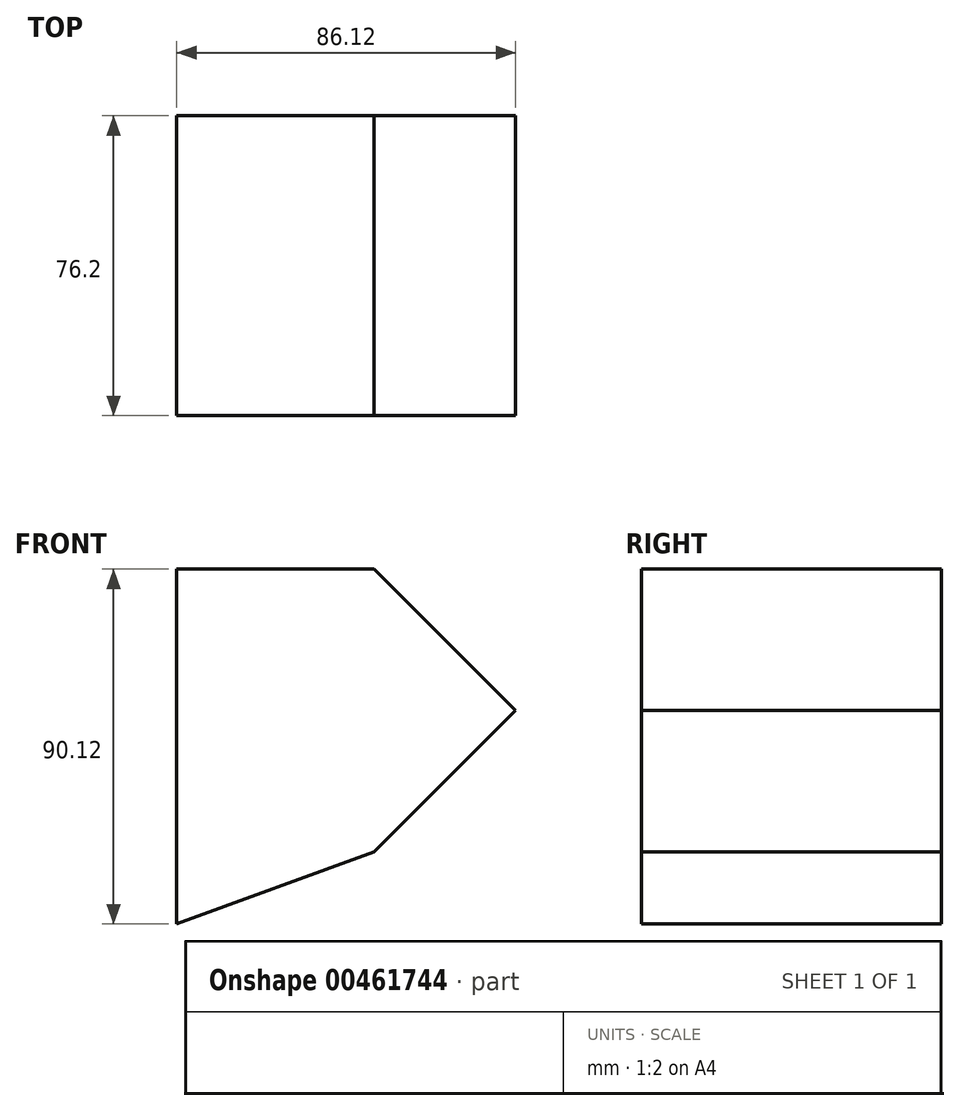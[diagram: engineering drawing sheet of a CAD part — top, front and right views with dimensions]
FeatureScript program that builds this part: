
annotation { "Feature Type Name" : "Feature", "Feature Type Description" : "" }
export const myFeature = defineFeature(function(context is Context, id is Id, definition is map)
    precondition{}
    {
        {
            var Q0;
            Q0=qCreatedBy(makeId("Front.planeOp"),FACE);
            var sketch = newSketch(context, id + "F0", { "sketchPlane" : qUnion([Q0])});
            skLineSegment(sketch, "E0.bottom", {"start": v(-50.2, 0) * mm, "end": v(39.92, 0) * mm});
            skLineSegment(sketch, "E0.top", {"start": v(-50.2, 54.27) * mm, "end": v(39.92, 54.27) * mm});
            skLineSegment(sketch, "E0.left", {"start": v(-50.2, 0) * mm, "end": v(-50.2, 54.27) * mm});
            skLineSegment(sketch, "E0.right", {"start": v(39.92, 0) * mm, "end": v(39.92, 54.27) * mm});
            skLineSegment(sketch, "E1", {"start": v(0, 0) * mm, "end": v(35.92, -35.92) * mm});
            skLineSegment(sketch, "E2", {"start": v(35.92, -35.92) * mm, "end": v(0, -71.84) * mm});
            skLineSegment(sketch, "E3", {"start": v(-50.2, 0) * mm, "end": v(-50.2, -90.12) * mm});
            skLineSegment(sketch, "E4", {"start": v(-50.2, -90.12) * mm, "end": v(0, -71.84) * mm});
            skSolve(sketch);
        }
        {
            var Q0;
            {var subQ1=sQuery(id+"F0.wireOp",EDGE,"E1");Q0=makeQuery(id+"F0.imprint","IMPRINT",FACE,{"disambiguationData":[TD([[makeQuery(id+"F0.imprint","IMPRINT",EDGE,{"derivedFrom":subQ1}),-1.0]])]});}
            extrude(context, id + "F1", {"entities" : qUnion([Q0]), "depth" : 76.2 * mm});
        }
    });
